# Revit family: Plumbing-Soap-Dispensers-Sloan-Valve-ESD-410_
name_source: partatom
category: Specialty Equipment
units: mm (PartAtom-declared; Revit-internal decimal feet)

## family parameters
Cut with Voids When Loaded = No
Host = Face
OmniClass Number = 23.40.20.21.34
OmniClass Title = Soap Holders, Dispensers
Part Type = Normal
Room Calculation Point = No
Round Connector Dimension = Use Diameter
Shared = No

## types (5) — shared parameters
Apparent Load = 216 VA
Assembly Code = D2010
CW Connection = Yes
Connector Description = Electrical Connection
Current = 2 A
Depth = 5.84 "
Edition number = 1
HW Connection = Yes
Height = 3.85 "
Keynote = 15410
Manufacturer = Sloan Valve
Number of Poles = 1
Power Factor = 1
Product data url = https://bimobject.com
URL = www.sloanvalve.com
Vent Connection = No
Voltage = 120 V
Waste Connection = No
Width = 1.9 "
zero-valued in all types: Default Elevation

## per-type parameters (varying)
| type | Description | Part Number | Product Material |
| ESD-410-BN | Sloan® Deck-Mounted Foam Soap Dispenser, Brushed Nickel Finish | 3346163 | Sloan Valve - Finish - Brushed Nickel |
| ESD-410-CP | Sloan® Deck-Mounted Foam Soap Dispenser, Polished Chrome Finish | 3346160 | Sloan Valve - Finish - Polished Chrome |
| ESD-410-GR | Sloan® Deck-Mounted Foam Soap Dispenser, Graphite Finish | 3346161 | Sloan Valve - Finish - Graphite |
| ESD-410-PB | Sloan® Deck-Mounted Foam Soap Dispenser, Polished Brass Finish | 3346162 | Sloan Valve - Finish - Polished Brass |
| ESD-410-SF | Sloan® Deck-Mounted Foam Soap Dispenser, Brushed Stainless Finish | 3346164 | Sloan Valve - Finish - Brushed Stainless Steel |

note: column(s) folded — value = type name in every type: Model

## geometry (parser evidence)
native form markers: Blend x4, Sweep x7
no freeform markers — native parametric forms only
